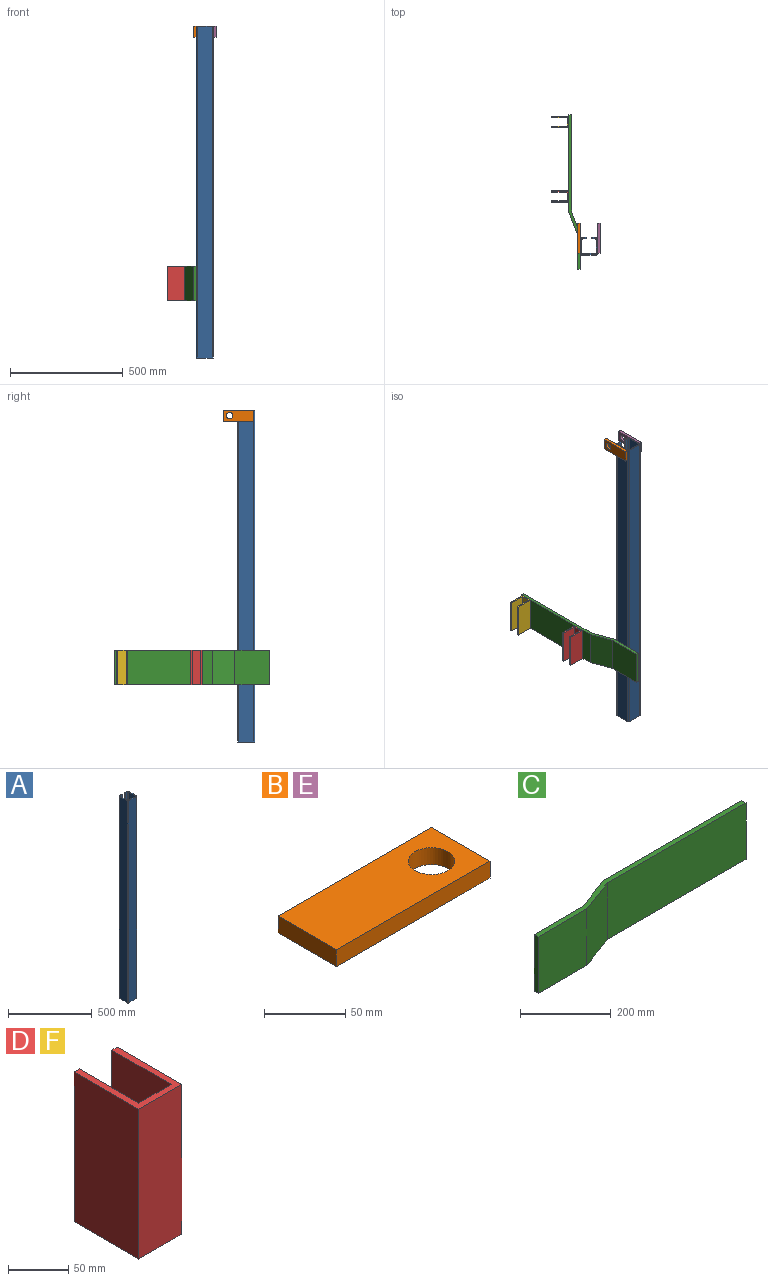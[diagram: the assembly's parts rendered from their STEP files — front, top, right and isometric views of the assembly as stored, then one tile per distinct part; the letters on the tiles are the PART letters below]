
ASSEMBLY  parts=6 mates=5
PART A: 22 faces, bbox 76.2x76.2x1473.2 mm
  f0: plane 1473.2x56.52mm, normal (1,0,0), area 83257.9mm2, adj f12,f13,f14,f20
  f1: plane 1473.2x15.57mm, normal (0,-1,0), area 22934.9mm2, adj f2,f12,f13,f14
  f2: plane 1473.2x4.76mm, normal (1,0,0), area 7016.1mm2, adj f1,f3,f12,f13
  f3: plane 1473.2x20.33mm, normal (0,1,0), area 29951mm2, adj f2,f12,f13,f18
  f4: plane 1473.2x66.04mm, normal (-1,0,0), area 97290.1mm2, adj f12,f13,f15,f18
  f5: plane 1473.2x66.04mm, normal (0,-1,0), area 97290.1mm2, adj f12,f13,f15,f16
  f6: plane 1473.2x66.04mm, normal (1,0,0), area 97290.1mm2, adj f12,f13,f16,f17
  f7: plane 1473.2x20.33mm, normal (0,1,0), area 29951mm2, adj f8,f12,f13,f17
  f8: plane 1473.2x4.76mm, normal (-1,0,0), area 7016.1mm2, adj f7,f9,f12,f13
  f9: plane 1473.2x15.57mm, normal (0,-1,0), area 22934.9mm2, adj f8,f12,f13,f21
  f10: plane 1473.2x56.52mm, normal (-1,0,0), area 83257.9mm2, adj f12,f13,f19,f21
  f11: plane 1473.2x56.52mm, normal (0,1,0), area 83257.9mm2, adj f12,f13,f19,f20
  f12: plane 76.2x76.2mm, normal (0,0,1), area 1240mm2, adj f0,f1,f2,f3,f4,f5,f6,f7
  f13: plane 76.2x76.2mm, normal (0,0,-1), area 1240mm2, adj f0,f1,f2,f3,f4,f5,f6,f7
  f14: cylinder r=5.08mm len=1473.2mm, axis (0,0,1), area 11755.6mm2, adj f0,f1,f12,f13
  f15: cylinder r=5.08mm len=1473.2mm, axis (0,0,1), area 11755.6mm2, adj f4,f5,f12,f13
  f16: cylinder r=5.08mm len=1473.2mm, axis (0,0,-1), area 11755.6mm2, adj f5,f6,f12,f13
  f17: cylinder r=5.08mm len=1473.2mm, axis (0,0,-1), area 11755.6mm2, adj f6,f7,f12,f13
  f18: cylinder r=5.08mm len=1473.2mm, axis (0,0,-1), area 11755.6mm2, adj f3,f4,f12,f13
  f19: cylinder r=5.08mm len=1473.2mm, axis (0,0,1), area 11755.6mm2, adj f10,f11,f12,f13
  f20: cylinder r=5.08mm len=1473.2mm, axis (0,0,-1), area 11755.6mm2, adj f0,f11,f12,f13
  f21: cylinder r=5.08mm len=1473.2mm, axis (0,0,-1), area 11755.6mm2, adj f9,f10,f12,f13
PART B: 7 faces, bbox 133.4x50.8x12.7 mm
  f0: plane 50.8x12.7mm, normal (-1,0,0), area 645.2mm2, adj f1,f3,f5,f6
  f1: plane 133.35x12.7mm, normal (0,-1,0), area 1693.5mm2, adj f0,f2,f5,f6
  f2: plane 50.8x12.7mm, normal (1,0,0), area 645.2mm2, adj f1,f3,f5,f6
  f3: plane 133.35x12.7mm, normal (0,1,0), area 1693.5mm2, adj f0,f2,f5,f6
  f4: cylinder r=14.29mm len=28.58mm, axis (0,0,-1), area 1140.1mm2, adj f5,f6
  f5: plane 133.35x50.8mm, normal (0,0,1), area 6132.9mm2, adj f0,f1,f2,f3,f4
  f6: plane 133.35x50.8mm, normal (0,0,-1), area 6132.9mm2, adj f0,f1,f2,f3,f4
PART C: 10 faces, bbox 685.8x50.8x152.4 mm
  f0: plane 152.4x152.4mm, normal (0,-1,0), area 23225.8mm2, adj f1,f7,f8,f9
  f1: plane 152.4x101.6mm, normal (0.35,-0.94,0), area 16536.7mm2, adj f0,f2,f8,f9
  f2: plane 431.8x152.4mm, normal (0,-1,0), area 65806.3mm2, adj f1,f3,f8,f9
  f3: plane 152.4x12.7mm, normal (1,0,0), area 1935.5mm2, adj f2,f4,f8,f9
  f4: plane 431.8x152.4mm, normal (0,1,0), area 65806.3mm2, adj f3,f5,f8,f9
  f5: plane 152.4x101.6mm, normal (-0.35,0.94,0), area 16536.7mm2, adj f4,f6,f8,f9
  f6: plane 152.4x152.4mm, normal (0,1,0), area 23225.8mm2, adj f5,f7,f8,f9
  f7: plane 152.4x12.7mm, normal (-1,0,0), area 1935.5mm2, adj f0,f6,f8,f9
  f8: plane 685.8x50.8mm, normal (0,0,1), area 8709.7mm2, adj f0,f1,f2,f3,f4,f5,f6,f7
  f9: plane 685.8x50.8mm, normal (0,0,-1), area 8709.7mm2, adj f0,f1,f2,f3,f4,f5,f6,f7
PART D: 10 faces, bbox 50.8x76.2x152.4 mm
  f0: plane 152.4x38.1mm, normal (0,1,0), area 5806.4mm2, adj f1,f7,f8,f9
  f1: plane 152.4x69.85mm, normal (1,0,0), area 10645.1mm2, adj f0,f2,f8,f9
  f2: plane 152.4x6.35mm, normal (0,1,0), area 967.7mm2, adj f1,f3,f8,f9
  f3: plane 152.4x76.2mm, normal (-1,0,0), area 11612.9mm2, adj f2,f4,f8,f9
  f4: plane 152.4x50.8mm, normal (0,-1,0), area 7741.9mm2, adj f3,f5,f8,f9
  f5: plane 152.4x76.2mm, normal (1,0,0), area 11612.9mm2, adj f4,f6,f8,f9
  f6: plane 152.4x6.35mm, normal (0,1,0), area 967.7mm2, adj f5,f7,f8,f9
  f7: plane 152.4x69.85mm, normal (-1,0,0), area 10645.1mm2, adj f0,f6,f8,f9
  f8: plane 76.2x50.8mm, normal (0,0,1), area 1209.7mm2, adj f0,f1,f2,f3,f4,f5,f6,f7
  f9: plane 76.2x50.8mm, normal (0,0,-1), area 1209.7mm2, adj f0,f1,f2,f3,f4,f5,f6,f7
PART E: same geometry as B
PART F: same geometry as D
PLACE A t=(101.2,-438.84,-432.57)mm
PLACE B rot(axis=(0.58,0.58,0.58),120deg) t=(88.5,-433.76,989.83)mm
PLACE C rot(axis=(0,0,1),90deg) t=(101.2,-502.34,-178.57)mm
PLACE D rot(axis=(0,0,1),90deg) t=(50.4,-203.89,-178.57)mm
PLACE E rot(axis=(0.58,0.58,0.58),120deg) t=(177.4,-433.76,989.83)mm
PLACE F rot(axis=(0,0,1),90deg) t=(50.4,126.31,-178.57)mm
MATE fastened F.f4 <-> C.f4  axis (1,0,0) through (50.4,151.71,-102.37)mm
MATE fastened A.f4 <-> C.f0  axis (-1,0,0) through (101.2,-400.74,304.03)mm
MATE fastened A.f6 <-> E.f6  axis (1,0,0) through (177.4,-433.76,1040.63)mm
MATE fastened D.f4 <-> C.f4  axis (1,0,0) through (50.4,-178.49,-102.37)mm
MATE fastened A.f4 <-> B.f5  axis (-1,0,0) through (101.2,-433.76,1040.63)mm
